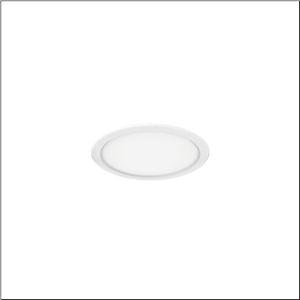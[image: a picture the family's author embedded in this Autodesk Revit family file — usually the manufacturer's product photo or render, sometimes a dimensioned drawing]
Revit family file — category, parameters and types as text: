
# Revit family: lunis_41_eco_51ds107d43a
name_source: partatom
category: Lighting Fixtures
units: mm (PartAtom-declared; Revit-internal decimal feet)

## family parameters
Cut with Voids When Loaded = No
Host = Face
Light Source = No
Part Type = Normal
Room Calculation Point = No
Round Connector Dimension = Use Diameter
Shared = No

## types (1)
- Lunis 41 ECO (1 x LED, 1460 lm, 14 W, 4000K)
    Apparent Load = 14 VA
    CIE Flux Codes = 47 80 97 100 100
    Color Rendering = 80
    Color Temperature = 4000K
    Default Elevation = 1800 mm
    Description = Lunis 41,  ECO, downlight, light emission: direct distribution, LED rated luminous flux: 1.460lm, light colour: 840, control gear: ECG, mains connection: 230V, AC, 50/60Hz, housing, round, of aluminium, coated, traffic white (RAL 9016), diameter: 166mm, recess depth: 54mm, protection rating (complete): IP20, protection rating (on room side): IP40, insulation class (complete): insulation class II (safety insulation), certification: CE, permissible ambient temperature for indoor applications: -20..+40°C, packaging unit: 1 piece
    Height = 0 mm  [stored 0 ft]
    Lamp = 1 x LED
    Lamp Light Flux = 1460 lm
    Lamp Power = 14 W
    Lamp count = 1
    Length = 165 mm
    Luminous efficacy = 104 lm/W
    Manufacturer = Siteco
    ModVariant = No
    Model = 51DS107D43A
    Mounting Place = Ceiling
    Mounting Type = Recessed
    Number of Poles = 1
    OnlyDefault = Yes
    Power Factor = 1
    Product Name = Lunis 41 ECO
    Product group = downlight
    ProductGroupID = 400
    Protection Class = Protection class II
    Protection Degree = IP 20
    RLX_Detail_Level = 1
    RLX_Emergency_Light_Flux = 0 lm
    RLX_Emergency_Type = 0
    RLX_Emergency_Type_DB = No
    RlxData = <blob elided: 25761 chars, md5=3c7e850f>
    Socket = socket
    Standby Power = 0 W
    System Light Flux = 1460 lm
    System Power = 14 W
    Type Comments = Product without accessories
    Type Image = l_1007041.jpg
    URL = http://relux.com
    VarID = ---
    Voltage = 0 V
    Weight = 0.00 kg
    Width = 0 mm  [stored 0 ft]

note: [stored X ft] marks values corroborated as IEEE doubles in the binary element streams (Revit-internal decimal feet)

## geometry (parser evidence)
native form markers: Blend x4, Sweep x11
no freeform markers — native parametric forms only
